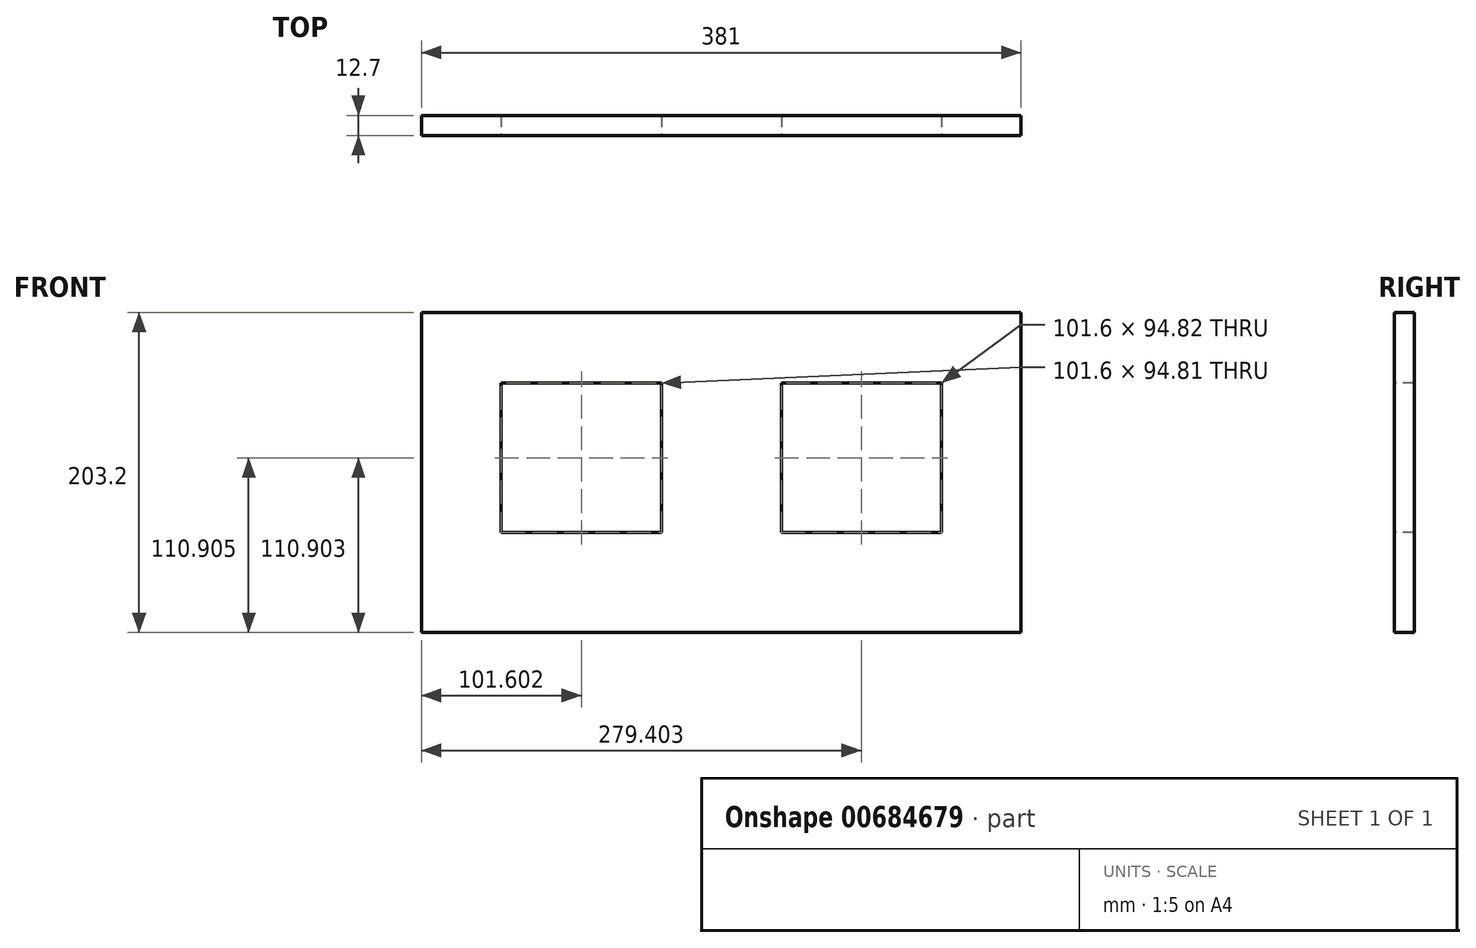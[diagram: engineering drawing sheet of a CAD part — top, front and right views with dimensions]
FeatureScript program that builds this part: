
annotation { "Feature Type Name" : "Feature", "Feature Type Description" : "" }
export const myFeature = defineFeature(function(context is Context, id is Id, definition is map)
    precondition{}
    {
        {
            var Q0;
            Q0=qCreatedBy(makeId("Front.planeOp"),FACE);
            var sketch = newSketch(context, id + "F0", { "sketchPlane" : qUnion([Q0])});
            skLineSegment(sketch, "E0.bottom", {"start": v(-139.04, 96.09) * mm, "end": v(241.96, 96.09) * mm});
            skLineSegment(sketch, "E0.top", {"start": v(-139.04, -107.11) * mm, "end": v(241.96, -107.11) * mm});
            skLineSegment(sketch, "E0.left", {"start": v(-139.04, 96.09) * mm, "end": v(-139.04, -107.11) * mm});
            skLineSegment(sketch, "E0.right", {"start": v(241.96, 96.09) * mm, "end": v(241.96, -107.11) * mm});
            skSolve(sketch);
        }
        {
            var Q0;
            Q0=qSketchRegion(id+"F0",true);
            extrude(context, id + "F1", {"entities" : qUnion([Q0]), "depth" : 12.7 * mm, "offsetDistance" : 25.4 * mm});
        }
        {
            var Q0;
            Q0=makeQuery(id+"F1.opExtrude","CAP_FACE",FACE,{"disambiguationData":[OSD([sQuery(id+"F0.wireOp",EDGE,"E0.bottom"),sQuery(id+"F0.wireOp",EDGE,"E0.top"),sQuery(id+"F0.wireOp",EDGE,"E0.left"),sQuery(id+"F0.wireOp",EDGE,"E0.right")])],"isStart":false});
            var sketch = newSketch(context, id + "F2", { "sketchPlane" : qUnion([Q0])});
            skSolve(sketch);
        }
        {
            var Q0;
            Q0=makeQuery(id+"F2.imprint","IMPRINT",FACE,{"disambiguationData":[TD([[makeQuery(id+"F2.imprint","IMPRINT",EDGE,{"derivedFrom":makeQuery(id+"F1.opExtrude","CAP_EDGE",EDGE,{"disambiguationData":[OSD([sQuery(id+"F0.wireOp",EDGE,"E0.bottom")])],"isStart":false})}),-1.0]])]});
            var sketch = newSketch(context, id + "F3", { "sketchPlane" : qUnion([Q0])});
            skLineSegment(sketch, "E1.bottom", {"start": v(-88.24, 51.2) * mm, "end": v(13.36, 51.2) * mm});
            skLineSegment(sketch, "E1.top", {"start": v(-88.24, -43.61) * mm, "end": v(13.36, -43.61) * mm});
            skLineSegment(sketch, "E1.left", {"start": v(-88.24, 51.2) * mm, "end": v(-88.24, -43.61) * mm});
            skLineSegment(sketch, "E1.right", {"start": v(13.36, 51.2) * mm, "end": v(13.36, -43.61) * mm});
            skLineSegment(sketch, "E2.bottom", {"start": v(89.56, 51.2) * mm, "end": v(191.16, 51.2) * mm});
            skLineSegment(sketch, "E2.top", {"start": v(89.56, -43.61) * mm, "end": v(191.16, -43.61) * mm});
            skLineSegment(sketch, "E2.left", {"start": v(89.56, 51.2) * mm, "end": v(89.56, -43.61) * mm});
            skLineSegment(sketch, "E2.right", {"start": v(191.16, 51.2) * mm, "end": v(191.16, -43.61) * mm});
            skSolve(sketch);
        }
        {
            var Q0;
            Q0=qSketchRegion(id+"F3",true);
            extrude(context, id + "F4", {"entities" : qUnion([Q0]), "operationType" : NewBodyOperationType.REMOVE, "endBound" : BoundingType.THROUGH_ALL, "oppositeDirection" : true, "depth" : 25.4 * mm, "offsetDistance" : 25.4 * mm});
        }
    });
